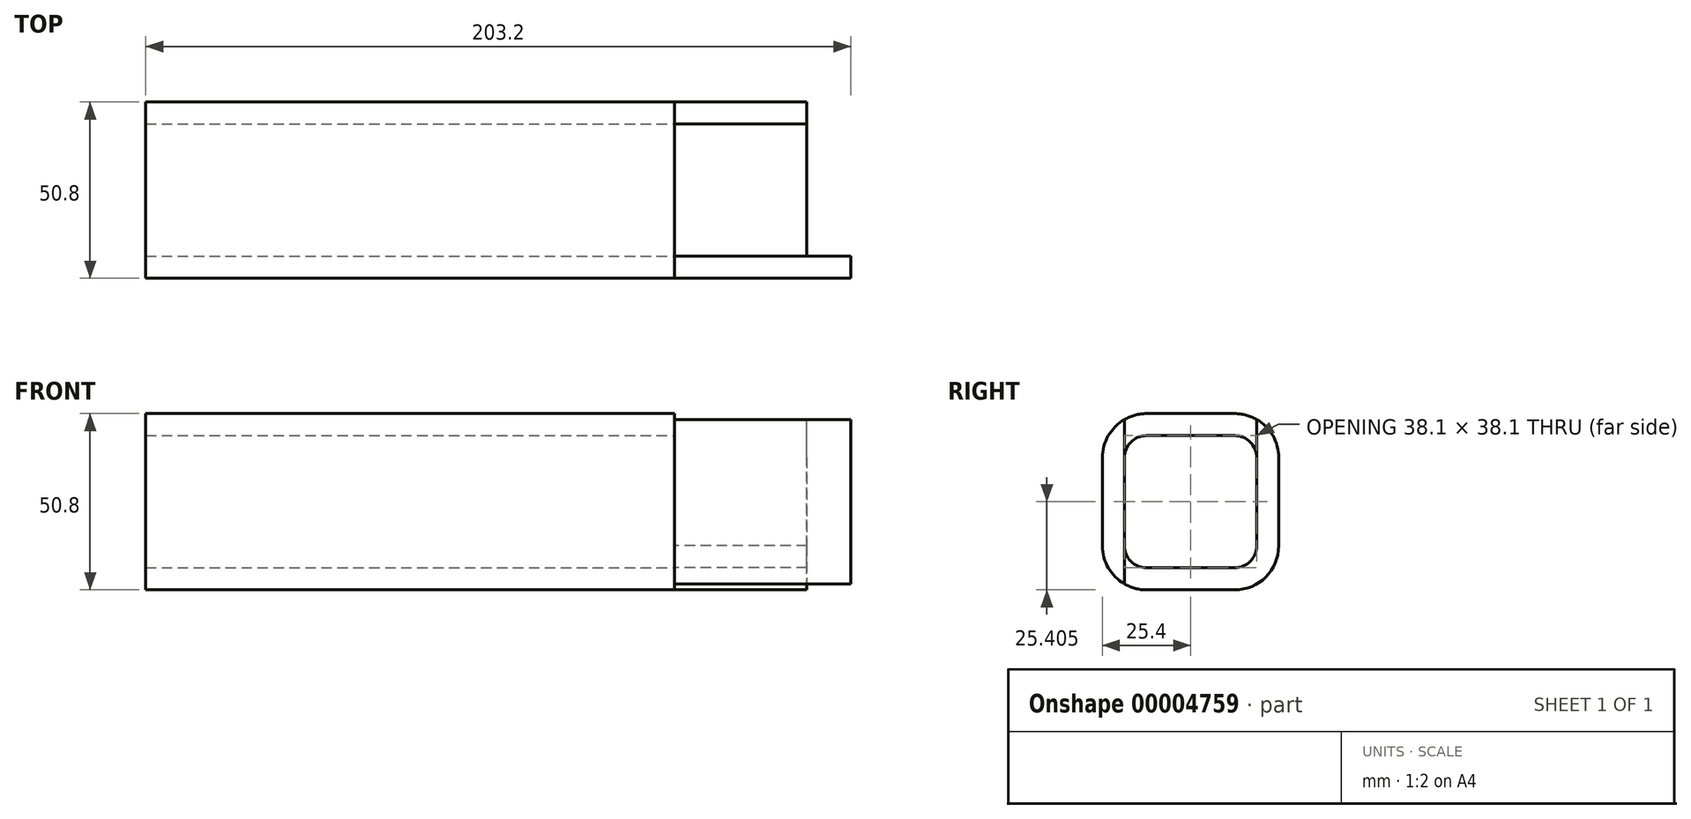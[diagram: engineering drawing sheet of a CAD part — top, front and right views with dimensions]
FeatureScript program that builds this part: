
annotation { "Feature Type Name" : "Feature", "Feature Type Description" : "" }
export const myFeature = defineFeature(function(context is Context, id is Id, definition is map)
    precondition{}
    {
        {
            var Q0;
            Q0=qCreatedBy(makeId("Top.planeOp"),FACE);
            var sketch = newSketch(context, id + "F0", { "sketchPlane" : qUnion([Q0])});
            skLineSegment(sketch, "E0", {"start": v(0, 0) * mm, "end": v(-304.8, -0.33) * mm});
            skSolve(sketch);
        }
        {
            var Q0;
            Q0=qCreatedBy(makeId("Right.planeOp"),FACE);
            var sketch = newSketch(context, id + "F1", { "sketchPlane" : qUnion([Q0])});
            skLineSegment(sketch, "E1", {"start": v(0.1, 17.8) * mm, "end": v(0.1, -17.7) * mm, "construction": true});
            skLineSegment(sketch, "E2", {"start": v(-15.03, -0.06) * mm, "end": v(20.26, -0.06) * mm, "construction": true});
            skLineSegment(sketch, "E3.bottom", {"start": v(12.8, 25.34) * mm, "end": v(-12.6, 25.34) * mm});
            skLineSegment(sketch, "E3.top", {"start": v(12.8, -25.46) * mm, "end": v(-12.6, -25.46) * mm});
            skLineSegment(sketch, "E3.left", {"start": v(25.5, 12.64) * mm, "end": v(25.5, -12.76) * mm});
            skLineSegment(sketch, "E3.right", {"start": v(-25.3, 12.64) * mm, "end": v(-25.3, -12.76) * mm});
            skPoint(sketch, "E3.middle", {"position": v(0.1, -0.06) * mm});
            skPoint(sketch, "E4.visualSharp", {"position": v(-25.3, 25.34) * mm});
            skArc(sketch, "E4.filletArc", {"start": v(-12.6, 25.34) * mm, "mid": v(-21.6, 21.62) * mm, "end": v(-25.3, 12.64) * mm});
            skPoint(sketch, "E5.visualSharp", {"position": v(25.5, 25.34) * mm});
            skArc(sketch, "E5.filletArc", {"start": v(25.5, 12.64) * mm, "mid": v(21.77, 21.62) * mm, "end": v(12.8, 25.34) * mm});
            skPoint(sketch, "E6.visualSharp", {"position": v(25.5, -25.46) * mm});
            skArc(sketch, "E6.filletArc", {"start": v(12.8, -25.46) * mm, "mid": v(21.77, -21.74) * mm, "end": v(25.5, -12.76) * mm});
            skPoint(sketch, "E7.visualSharp", {"position": v(-25.3, -25.46) * mm});
            skArc(sketch, "E7.filletArc", {"start": v(-25.3, -12.76) * mm, "mid": v(-21.6, -21.74) * mm, "end": v(-12.6, -25.46) * mm});
            skArc(sketch, "E8.0", {"start": v(19.14, 12.64) * mm, "mid": v(17.28, 17.13) * mm, "end": v(12.8, 19) * mm});
            skLineSegment(sketch, "E8.1", {"start": v(19.14, 12.64) * mm, "end": v(19.14, -12.76) * mm});
            skLineSegment(sketch, "E8.2", {"start": v(12.8, 19) * mm, "end": v(-12.6, 19) * mm});
            skArc(sketch, "E8.3", {"start": v(12.8, -19.1) * mm, "mid": v(17.28, -17.25) * mm, "end": v(19.14, -12.76) * mm});
            skArc(sketch, "E8.4", {"start": v(-12.6, 19) * mm, "mid": v(-17.1, 17.13) * mm, "end": v(-18.96, 12.64) * mm});
            skLineSegment(sketch, "E8.5", {"start": v(-18.96, 12.64) * mm, "end": v(-18.96, -12.76) * mm});
            skArc(sketch, "E8.6", {"start": v(-18.96, -12.76) * mm, "mid": v(-17.1, -17.25) * mm, "end": v(-12.6, -19.1) * mm});
            skLineSegment(sketch, "E8.7", {"start": v(12.8, -19.1) * mm, "end": v(-12.6, -19.1) * mm});
            skLineSegment(sketch, "E9", {"start": v(-25.3, -12.76) * mm, "end": v(-18.96, -12.76) * mm});
            skLineSegment(sketch, "E10", {"start": v(19.14, -12.76) * mm, "end": v(25.5, -12.76) * mm});
            skLineSegment(sketch, "E11", {"start": v(-12.6, -19.1) * mm, "end": v(-12.6, -25.46) * mm});
            skLineSegment(sketch, "E12", {"start": v(12.8, -19.1) * mm, "end": v(12.8, -25.46) * mm});
            skLineSegment(sketch, "E13", {"start": v(-18.96, 12.64) * mm, "end": v(-18.96, 23.64) * mm});
            skLineSegment(sketch, "E14", {"start": v(19.14, 12.64) * mm, "end": v(19.14, 23.64) * mm});
            skLineSegment(sketch, "E15", {"start": v(-12.6, 19) * mm, "end": v(-12.6, 25.34) * mm});
            skLineSegment(sketch, "E16", {"start": v(12.8, 19) * mm, "end": v(12.8, 25.34) * mm});
            skLineSegment(sketch, "E17", {"start": v(-18.96, -12.76) * mm, "end": v(-18.96, -23.75) * mm});
            skLineSegment(sketch, "E18", {"start": v(19.14, -12.76) * mm, "end": v(19.14, -23.75) * mm});
            skSolve(sketch);
        }
        {
            var Q0;
            Q0=makeQuery(id+"F1.imprint","IMPRINT",FACE,{"disambiguationData":[TD([[makeQuery(id+"F1.imprint","IMPRINT",EDGE,{"derivedFrom":sQuery(id+"F1.wireOp",EDGE,"E7.filletArc")}),1.0]])]});
            var Q1;
            {var subQ1=sQuery(id+"F1.wireOp",EDGE,"E3.right");Q1=makeQuery(id+"F1.imprint","IMPRINT",FACE,{"disambiguationData":[TD([[makeQuery(id+"F1.imprint","IMPRINT",EDGE,{"derivedFrom":subQ1}),1.0]])]});}
            extrude(context, id + "F2", {"entities" : qUnion([Q0, Q1]), "depth" : 50.8 * mm, "offsetDistance" : 25.4 * mm});
        }
        {
            var Q0;
            {var subQ0=sQuery(id+"F1.wireOp",EDGE,"E10");Q0=makeQuery(id+"F1.imprint","IMPRINT",FACE,{"disambiguationData":[TD([[makeQuery(id+"F1.imprint","IMPRINT",EDGE,{"derivedFrom":subQ0}),-1.0]])]});}
            var Q1;
            Q1=makeQuery(id+"F1.imprint","IMPRINT",FACE,{"disambiguationData":[TD([[makeQuery(id+"F1.imprint","IMPRINT",EDGE,{"derivedFrom":sQuery(id+"F1.wireOp",EDGE,"E3.top")}),-1.0]])]});
            var Q2;
            {var subQ0=sQuery(id+"F1.wireOp",EDGE,"E3.left");Q2=makeQuery(id+"F1.imprint","IMPRINT",FACE,{"disambiguationData":[TD([[makeQuery(id+"F1.imprint","IMPRINT",EDGE,{"derivedFrom":subQ0}),-1.0]])]});}
            var Q3;
            Q3=makeQuery(id+"F1.imprint","IMPRINT",FACE,{"disambiguationData":[TD([[makeQuery(id+"F1.imprint","IMPRINT",EDGE,{"derivedFrom":sQuery(id+"F1.wireOp",EDGE,"E8.3")}),-1.0]])]});
            var Q4;
            Q4=makeQuery(id+"F1.imprint","IMPRINT",FACE,{"disambiguationData":[TD([[makeQuery(id+"F1.imprint","IMPRINT",EDGE,{"derivedFrom":sQuery(id+"F1.wireOp",EDGE,"E8.6")}),-1.0]])]});
            extrude(context, id + "F3", {"entities" : qUnion([Q0, Q1, Q2, Q3, Q4]), "depth" : 38.1 * mm, "offsetDistance" : 25.4 * mm});
        }
        {
            var Q0;
            Q0=makeQuery(id+"F1.imprint","IMPRINT",FACE,{"disambiguationData":[TD([[makeQuery(id+"F1.imprint","IMPRINT",EDGE,{"derivedFrom":sQuery(id+"F1.wireOp",EDGE,"E3.bottom")}),1.0]])]});
            var Q1;
            Q1=makeQuery(id+"F1.imprint","IMPRINT",FACE,{"disambiguationData":[TD([[makeQuery(id+"F1.imprint","IMPRINT",EDGE,{"derivedFrom":sQuery(id+"F1.wireOp",EDGE,"E8.4")}),-1.0]])]});
            var Q2;
            {var subQ1=sQuery(id+"F1.wireOp",EDGE,"E3.right");Q2=makeQuery(id+"F1.imprint","IMPRINT",FACE,{"disambiguationData":[TD([[makeQuery(id+"F1.imprint","IMPRINT",EDGE,{"derivedFrom":subQ1}),1.0]])]});}
            var Q3;
            {var subQ0=sQuery(id+"F1.wireOp",EDGE,"E9");Q3=makeQuery(id+"F1.imprint","IMPRINT",FACE,{"disambiguationData":[TD([[makeQuery(id+"F1.imprint","IMPRINT",EDGE,{"derivedFrom":subQ0}),-1.0]])]});}
            var Q4;
            Q4=makeQuery(id+"F1.imprint","IMPRINT",FACE,{"disambiguationData":[TD([[makeQuery(id+"F1.imprint","IMPRINT",EDGE,{"derivedFrom":sQuery(id+"F1.wireOp",EDGE,"E8.6")}),-1.0]])]});
            var Q5;
            Q5=makeQuery(id+"F1.imprint","IMPRINT",FACE,{"disambiguationData":[TD([[makeQuery(id+"F1.imprint","IMPRINT",EDGE,{"derivedFrom":sQuery(id+"F1.wireOp",EDGE,"E3.top")}),-1.0]])]});
            var Q6;
            Q6=makeQuery(id+"F1.imprint","IMPRINT",FACE,{"disambiguationData":[TD([[makeQuery(id+"F1.imprint","IMPRINT",EDGE,{"derivedFrom":sQuery(id+"F1.wireOp",EDGE,"E8.3")}),-1.0]])]});
            var Q7;
            {var subQ0=sQuery(id+"F1.wireOp",EDGE,"E10");Q7=makeQuery(id+"F1.imprint","IMPRINT",FACE,{"disambiguationData":[TD([[makeQuery(id+"F1.imprint","IMPRINT",EDGE,{"derivedFrom":subQ0}),-1.0]])]});}
            var Q8;
            {var subQ0=sQuery(id+"F1.wireOp",EDGE,"E3.left");Q8=makeQuery(id+"F1.imprint","IMPRINT",FACE,{"disambiguationData":[TD([[makeQuery(id+"F1.imprint","IMPRINT",EDGE,{"derivedFrom":subQ0}),-1.0]])]});}
            var Q9;
            Q9=makeQuery(id+"F1.imprint","IMPRINT",FACE,{"disambiguationData":[TD([[makeQuery(id+"F1.imprint","IMPRINT",EDGE,{"derivedFrom":sQuery(id+"F1.wireOp",EDGE,"E8.0")}),-1.0]])]});
            extrude(context, id + "F4", {"entities" : qUnion([Q0, Q1, Q2, Q3, Q4, Q5, Q6, Q7, Q8, Q9]), "oppositeDirection" : true, "depth" : 152.4 * mm, "offsetDistance" : 25.4 * mm});
        }
    });
